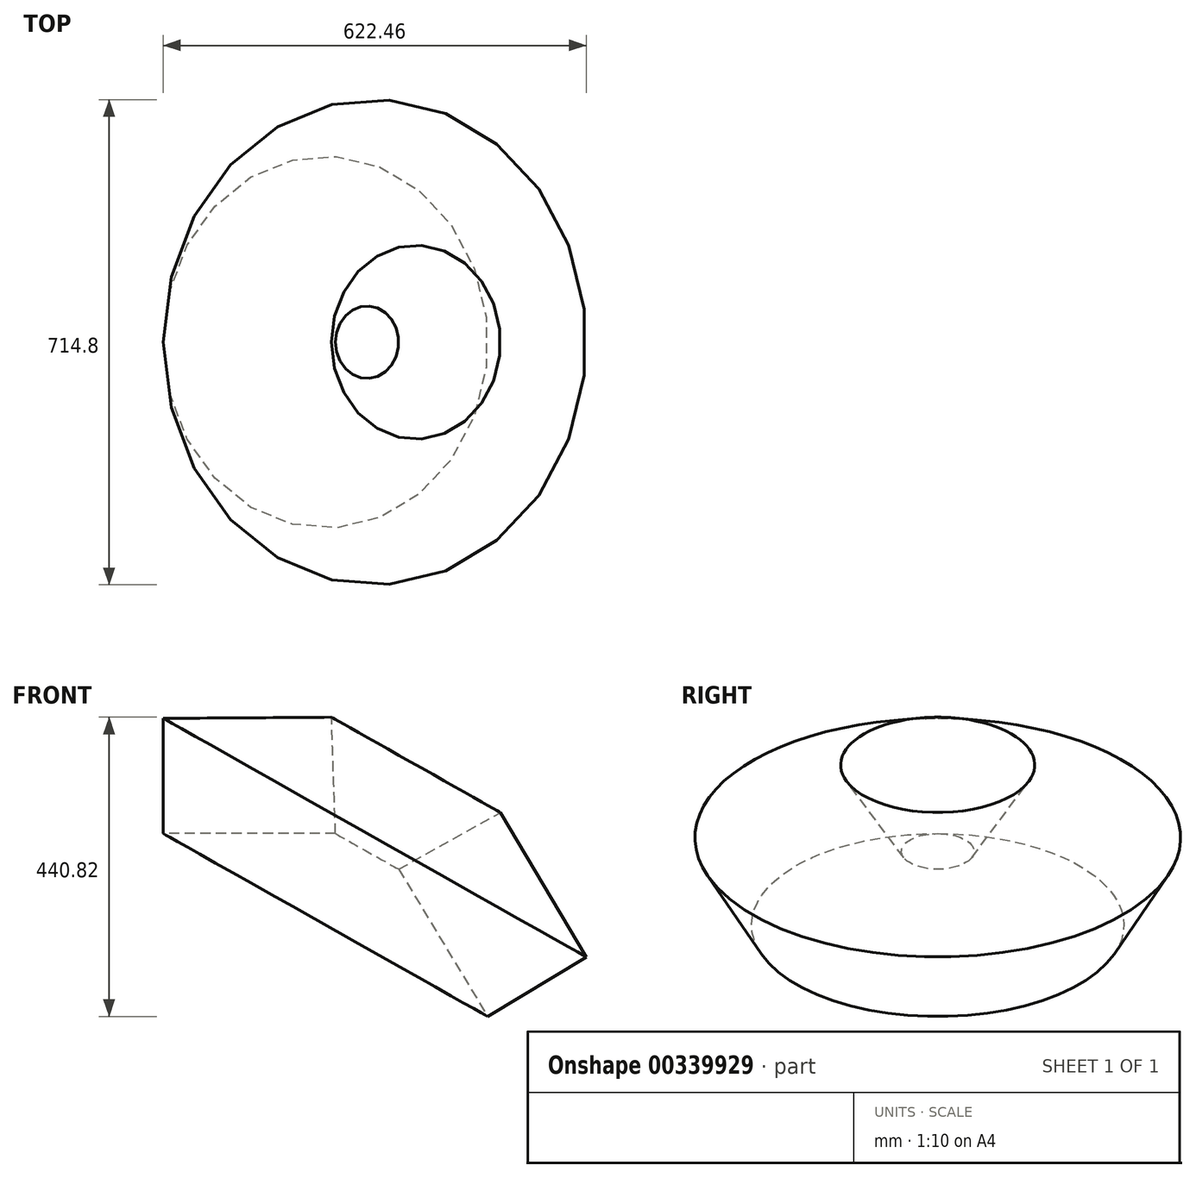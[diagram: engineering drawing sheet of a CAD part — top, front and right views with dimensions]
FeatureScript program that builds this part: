
annotation { "Feature Type Name" : "Feature", "Feature Type Description" : "" }
export const myFeature = defineFeature(function(context is Context, id is Id, definition is map)
    precondition{}
    {
        {
            var Q0;
            Q0=qCreatedBy(makeId("Front.planeOp"),FACE);
            var sketch = newSketch(context, id + "F0", { "sketchPlane" : qUnion([Q0])});
            skLineSegment(sketch, "E0", {"start": v(-169.64, 99.55) * mm, "end": v(-169.64, -70.1) * mm});
            skLineSegment(sketch, "E1", {"start": v(-169.64, -70.1) * mm, "end": v(83.64, -70.1) * mm});
            skLineSegment(sketch, "E2", {"start": v(83.64, -70.1) * mm, "end": v(77.75, 101.32) * mm});
            skLineSegment(sketch, "E3", {"start": v(77.75, 101.32) * mm, "end": v(-169.64, 99.55) * mm});
            skSolve(sketch);
        }
        {
            var Q0;
            Q0=makeQuery(id+"F0.imprint","IMPRINT",FACE,{"disambiguationData":[TD([[makeQuery(id+"F0.imprint","IMPRINT",EDGE,{"derivedFrom":sQuery(id+"F0.wireOp",EDGE,"E0")}),1.0]])]});
            var sketch = newSketch(context, id + "F1", { "sketchPlane" : qUnion([Q0])});
            skLineSegment(sketch, "E4", {"start": v(110.68, -130.9) * mm, "end": v(196.73, 21.53) * mm});
            skSolve(sketch);
        }
        {
            var Q0;
            Q0=makeQuery(id+"F1.imprint","IMPRINT",FACE,{"disambiguationData":[TD([[makeQuery(id+"F1.imprint","IMPRINT",EDGE,{"derivedFrom":makeQuery(id+"F0.imprint","IMPRINT",EDGE,{"derivedFrom":sQuery(id+"F0.wireOp",EDGE,"E0")})}),1.0]])]});
            var Q1;
            Q1=sQuery(id+"F1.wireOp",EDGE,"E4");
            revolve(context, id + "F2", {"entities" : qUnion([Q0]), "axis" : qUnion([Q1]), "revolveType" : RevolveType.FULL});
        }
    });
